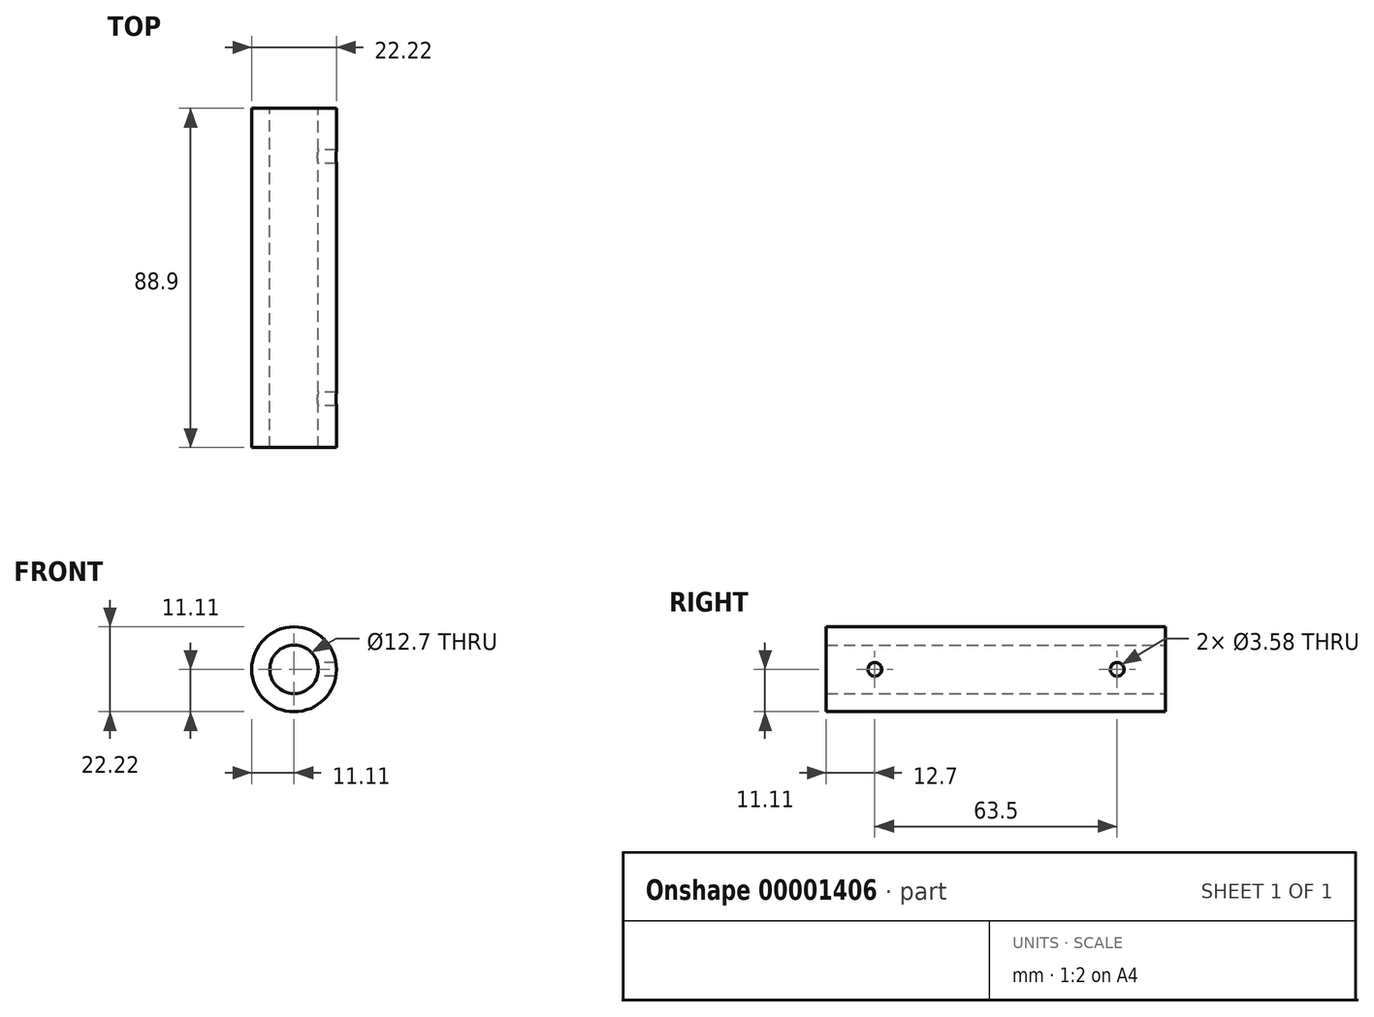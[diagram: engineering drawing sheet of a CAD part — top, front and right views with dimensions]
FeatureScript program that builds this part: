
annotation { "Feature Type Name" : "Feature", "Feature Type Description" : "" }
export const myFeature = defineFeature(function(context is Context, id is Id, definition is map)
    precondition{}
    {
        {
            var Q0;
            Q0=qCreatedBy(makeId("Front.planeOp"),FACE);
            var sketch = newSketch(context, id + "F0", { "sketchPlane" : qUnion([Q0])});
            skCircle(sketch, "E0", {"center": v(0, 0) * mm, "radius": 11.11 * mm});
            skCircle(sketch, "E1", {"center": v(0, 0) * mm, "radius": 6.35 * mm});
            skSolve(sketch);
        }
        {
            var Q0;
            Q0 = qSketchRegion(id + "F0", true);
            extrude(context, id + "F1", {"entities" : qUnion([Q0]), "endBound" : BoundingType.SYMMETRIC, "depth" : 88.9 * mm});
        }
        {
            var Q0;
            Q0=qCreatedBy(makeId("Right.planeOp"),FACE);
            var sketch = newSketch(context, id + "F2", { "sketchPlane" : qUnion([Q0])});
            skCircle(sketch, "E2", {"center": v(31.75, 0) * mm, "radius": 1.8 * mm});
            skCircle(sketch, "E3", {"center": v(-31.75, 0) * mm, "radius": 1.8 * mm});
            skSolve(sketch);
        }
        {
            var Q0;
            Q0 = qSketchRegion(id + "F2", true);
            extrude(context, id + "F3", {"entities" : qUnion([Q0]), "operationType" : NewBodyOperationType.REMOVE, "endBound" : BoundingType.THROUGH_ALL, "depth" : 25.4 * mm});
        }
    });
